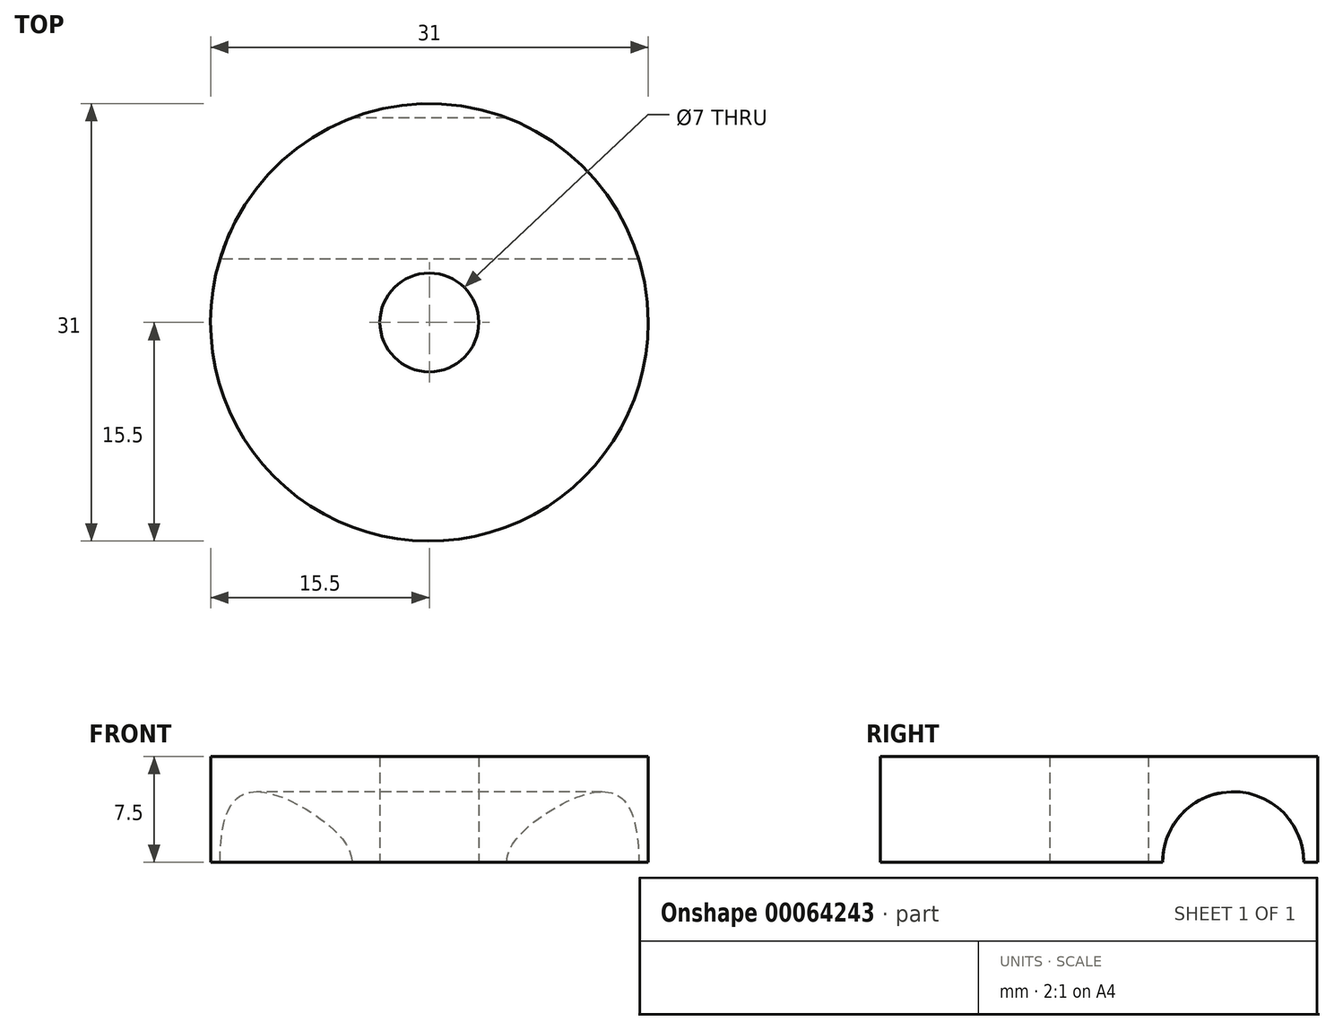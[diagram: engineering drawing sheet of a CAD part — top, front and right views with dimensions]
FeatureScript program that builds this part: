
annotation { "Feature Type Name" : "Feature", "Feature Type Description" : "" }
export const myFeature = defineFeature(function(context is Context, id is Id, definition is map)
    precondition{}
    {
        {
            var Q0;
            Q0=qCreatedBy(makeId("Top.planeOp"),FACE);
            var sketch = newSketch(context, id + "F0", { "sketchPlane" : qUnion([Q0])});
            skCircle(sketch, "E0", {"center": v(0, 0) * mm, "radius": 15.5 * mm});
            skSolve(sketch);
        }
        {
            var Q0;
            Q0=qCreatedBy(makeId("Top.planeOp"),FACE);
            var sketch = newSketch(context, id + "F1", { "sketchPlane" : qUnion([Q0])});
            skPoint(sketch, "E1", {"position": v(0, 0) * mm});
            skSolve(sketch);
        }
        {
            var Q0;
            Q0=makeQuery(id+"F0.imprint","IMPRINT",FACE,{"disambiguationData":[TD([[makeQuery(id+"F0.imprint","IMPRINT",EDGE,{"derivedFrom":sQuery(id+"F0.wireOp",EDGE,"E0")}),1.0]])]});
            extrude(context, id + "F2", {"entities" : qUnion([Q0]), "depth" : 7.5 * mm});
        }
        {
            var Q0;
            Q0=qCreatedBy(makeId("Right.planeOp"),FACE);
            var sketch = newSketch(context, id + "F3", { "sketchPlane" : qUnion([Q0])});
            skCircle(sketch, "E2", {"center": v(9.5, 0) * mm, "radius": 5 * mm});
            skSolve(sketch);
        }
        {
            var Q0;
            Q0=makeQuery(id+"F3.imprint","IMPRINT",FACE,{"disambiguationData":[TD([[makeQuery(id+"F3.imprint","IMPRINT",EDGE,{"derivedFrom":sQuery(id+"F3.wireOp",EDGE,"E2")}),1.0]])]});
            extrude(context, id + "F4", {"entities" : qUnion([Q0]), "operationType" : NewBodyOperationType.REMOVE, "endBound" : BoundingType.SYMMETRIC, "depth" : 40 * mm});
        }
        {
            var Q0;
            Q0=sQuery(id+"F1.wireOp",VERTEX,"E1");
            var Q1;
            Q1=makeQuery(id+"F2.opExtrude","SWEPT_BODY",BODY,{"disambiguationData":[OSD([sQuery(id+"F0.wireOp",EDGE,"E0")])]});
            hole(context, id + "F5", {"style" : HoleStyle.SIMPLE, "holeDiameter" : 7 * mm, "endStyle" : HoleEndStyle.THROUGH, "oppositeDirection" : true, "locations" : qUnion([Q0]), "scope" : qUnion([Q1])});
        }
    });
